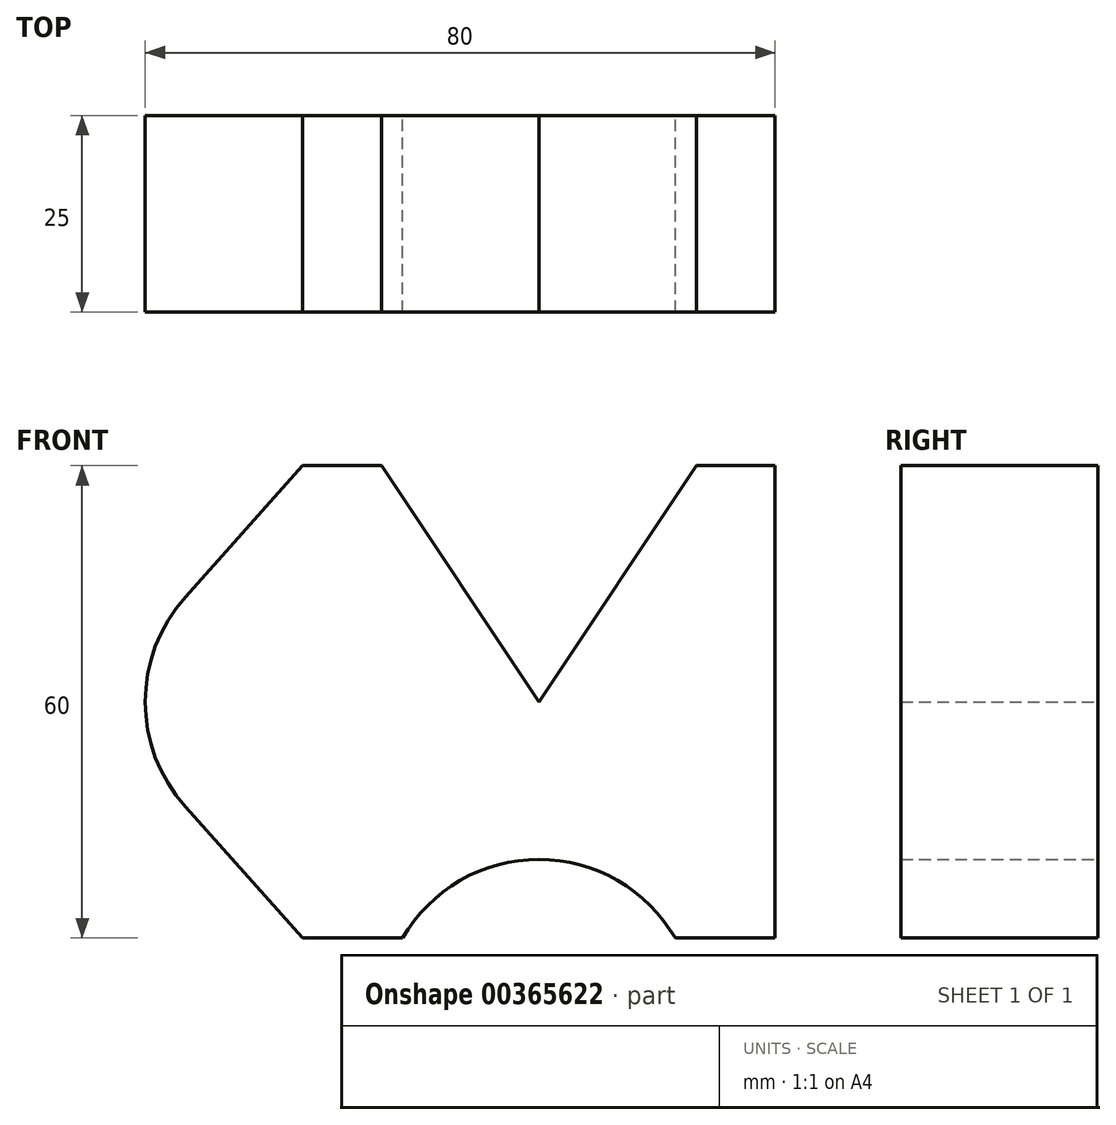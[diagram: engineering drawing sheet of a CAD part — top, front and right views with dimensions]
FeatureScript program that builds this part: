
annotation { "Feature Type Name" : "Feature", "Feature Type Description" : "" }
export const myFeature = defineFeature(function(context is Context, id is Id, definition is map)
    precondition{}
    {
        {
            var Q0;
            Q0=qCreatedBy(makeId("Front.planeOp"),FACE);
            var sketch = newSketch(context, id + "F0", { "sketchPlane" : qUnion([Q0])});
            skLineSegment(sketch, "E0", {"start": v(-44.9, 13.33) * mm, "end": v(-30, 30) * mm});
            skLineSegment(sketch, "E1", {"start": v(-30, 30) * mm, "end": v(-20, 30) * mm});
            skLineSegment(sketch, "E2", {"start": v(-20, 30) * mm, "end": v(0, 0) * mm});
            skLineSegment(sketch, "E3", {"start": v(0, 0) * mm, "end": v(20, 30) * mm});
            skLineSegment(sketch, "E4", {"start": v(20, 30) * mm, "end": v(30, 30) * mm});
            skLineSegment(sketch, "E5", {"start": v(30, 30) * mm, "end": v(30, -30) * mm});
            skLineSegment(sketch, "E6", {"start": v(30, -30) * mm, "end": v(17.32, -30) * mm});
            skArc(sketch, "E7", {"start": v(17.32, -30) * mm, "mid": v(0, -20) * mm, "end": v(-17.32, -30) * mm});
            skLineSegment(sketch, "E8", {"start": v(-17.32, -30) * mm, "end": v(-30, -30) * mm});
            skLineSegment(sketch, "E9", {"start": v(-30, -30) * mm, "end": v(-44.9, -13.33) * mm});
            skArc(sketch, "E10", {"start": v(-44.9, 13.33) * mm, "mid": v(-50, 0) * mm, "end": v(-44.9, -13.33) * mm});
            skLineSegment(sketch, "E11", {"start": v(-30, 30) * mm, "end": v(-30, -30) * mm, "construction": true});
            skSolve(sketch);
        }
        {
            var Q0;
            Q0=makeQuery(id+"F0.imprint","IMPRINT",FACE,{"disambiguationData":[TD([[makeQuery(id+"F0.imprint","IMPRINT",EDGE,{"derivedFrom":sQuery(id+"F0.wireOp",EDGE,"E0")}),-1.0]])]});
            extrude(context, id + "F1", {"entities" : qUnion([Q0]), "depth" : 25 * mm});
        }
    });
